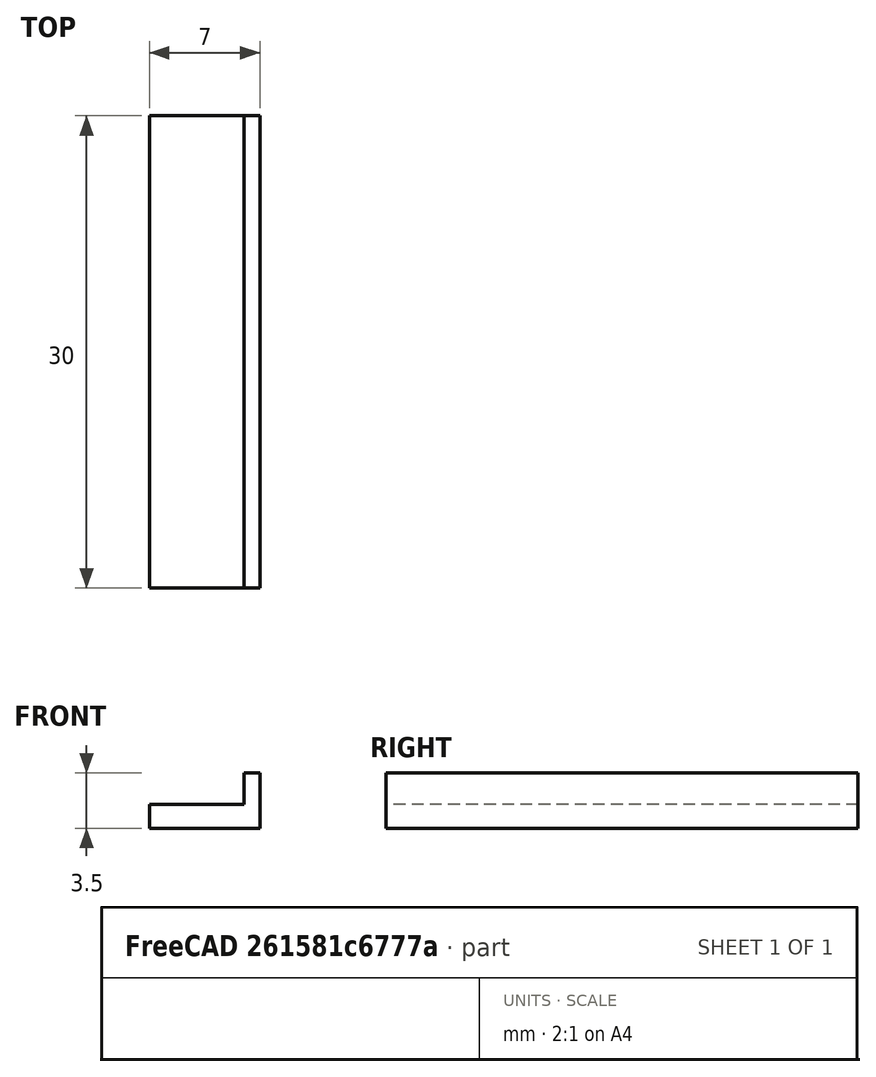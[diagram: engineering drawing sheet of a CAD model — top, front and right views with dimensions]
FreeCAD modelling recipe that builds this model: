
FCSTD DOCUMENT  (FreeCAD 2023.521R14555 (Git shallow))
Label: Z_stop
License: All rights reserved
LicenseURL: https://en.wikipedia.org/wiki/All_rights_reserved
objects: Sketcher::SketchObject×1, PartDesign::Pad×1, PartDesign::Body×1
note: 6 computed .brp shape members not serialized (recipe doc carries the construction recipe); baked Part::Feature solids carry a one-line shape summary decoded from their .brp

FEATURE [Sketcher::SketchObject] Sketch
  ArcFitTolerance = 1e-06
  AttachmentSupport = -> [XZ_Plane]
  ExternalBSplineMaxDegree = 5
  ExternalBSplineTolerance = 0.0001
  FixShape = 1
  FullyConstrained = true
  InternalTolerance = 1e-06
  InvalidShape = false
  MakeInternals = false
  MapMode = 5
  Placement = pos=(0,0,0) rot=(1,0,0;1.5708rad)
  Support = -> [XZ_Plane]
  TreeRank = 11
  ValidateShape = false
  sketch-geometry (6):
    g0: LineSegment StartX=0 StartY=0 StartZ=0 EndX=-7 EndY=0 EndZ=0
    g1: LineSegment StartX=-7 StartY=0 StartZ=0 EndX=-7 EndY=1.5 EndZ=0
    g2: LineSegment StartX=-7 StartY=1.5 StartZ=0 EndX=-1 EndY=1.5 EndZ=0
    g3: LineSegment StartX=-1 StartY=1.5 StartZ=0 EndX=-1 EndY=3.5 EndZ=0
    g4: LineSegment StartX=-1 StartY=3.5 StartZ=0 EndX=0 EndY=3.5 EndZ=0
    g5: LineSegment StartX=0 StartY=3.5 StartZ=0 EndX=0 EndY=0 EndZ=0
  constraints (17):
    c: Coincident(g0,g-1)
    c: PointOnObject(g0,g-1)
    c: Coincident(g1,g0)
    c: Horizontal(g2)
    c: Coincident(g3,g2)
    c: Vertical(g3)
    c: Coincident(g4,g3)
    c: PointOnObject(g4,g-2)
    c: Horizontal(g4)
    c: Coincident(g5,g4)
    c: Coincident(g5,g0)
    c: Coincident(g1,g2)
    c: DistanceX(g2,g0) = 1
    c: DistanceX(g2,g2) = 6
    c: Vertical(g1)
    c: DistanceY(g1,g1) = 1.5
    c: DistanceY(g3,g3) = 2
FEATURE [PartDesign::Pad] Pad
  AddSubType = 0
  AlongSketchNormal = false
  AutoTaperInnerAngle = true
  CheckUpToFaceLimits = true
  ClaimChildren = false
  Direction = (0,-1,2e-16)
  Fit = 0
  FitJoin = 0
  FixShape = 1
  InnerFit = 0
  InnerFitJoin = 0
  InvalidShape = false
  Length = 30
  Length2 = 10
  Linearize = true
  NewSolid = false
  Profile = -> Sketch
  ReferenceAxis = -> Sketch [N_Axis]
  Refine = true
  Suppress = false
  TaperInnerAngle = 0
  TaperInnerAngleRev = 0
  TreeRank = 12
  Type = 0
  ValidateShape = true
  _ProfileBasedVersion = 1
FEATURE [PartDesign::Body] Body
  AutoGroupSolids = false
  ClaimAllChildren = false
  ExportMode = 0
  FixShape = 1
  Group = -> [Sketch,Pad]
  InvalidShape = false
  Origin = -> Origin
  Tip = -> Pad
  TreeRank = 10
  ValidateShape = false
  _ExportChildren = -> [Pad]
  _GroupVersion = 1
